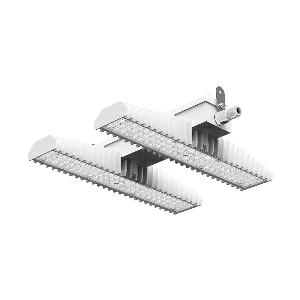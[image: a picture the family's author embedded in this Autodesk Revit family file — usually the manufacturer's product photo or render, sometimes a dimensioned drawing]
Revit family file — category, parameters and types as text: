
# Revit family: 3f_filippi_-_3f_lem_concentrato_3f_filippi_-_58888_-_3f_lem_2_led_100_cr_conc
name_source: partatom
category: Lighting Fixtures
units: mm (PartAtom-declared; Revit-internal decimal feet)

## family parameters
Cut with Voids When Loaded = No
Host = Face
Light Source = No
Part Type = Normal
Room Calculation Point = No
Round Connector Dimension = Use Diameter
Shared = No

## types (1)
- 3F Filippi - 3F LEM Concentrato (1 x LED, 16270 lm, 109 W, 4000 K)
    Apparent Load = 109 VA
    Approval mark = CE
    CIE Flux Codes = 83 96 99 100 100
    Color Rendering = 80
    Color Temperature = 4000 K
    Control Gear = Electronic ballast
    Default Elevation = 1800 mm
    Description = Industrial luminaire with high light output and high luminous efficiency designed with the most innovative technologies for environments with temperature up to 55°C.

ILLUMINOTECHNICAL
Luminous efficiency 100% (DLOR 100%, ULOR 0%).
Initial luminous flux of the luminaire 16270 lm.
Direct symmetric narrow distribution: the illuminated area has a elliptical shape.
Installation Interdistance Transv.D = 0.52 x hu - Long.D = 1.16 x hu.
Tabular UGR (CIE 117 - 4H-8H; S=0.25H; 70/50/20): RUG 16.8 - 20.6.
Beam angle: 31° - 73°.
Luminous efficacy 149 lm/W.
Lifetime (L93/B10): 30000 h. (tq+25°C)
Lifetime (L90/B10): 50000 h. (tq+25°C)
Lifetime (L85/B10): 80000 h. (tq+25°C)
Lifetime (L80/B10): 100000 h. (tq+25°C)
Lifetime (L85/B10): 50000 h. (tq+55°C)
Sudden decreased luminous flux after 50000 hours: 0% (C0).
Photobiological safety in compliance with IEC/TR 62778: RG0 risk exempt, (IEC 62471).
In compliance with IEC/EN 62722-2-1 - IEC/EN 62717 standards.

SOURCE
2 Mid-Power linear LED modules 50W/840.
Energy efficiency class (UE 2019/2020 - UE 2019/2015): C.
CIE 13.3 Colour rendering index: CRI >80 (R9 <50%).
IES TM-30 Fidelity Index: Rf = 84 Rg = 95.
CCT nominal colour temperature 4000 K.
Colour initial tolerance (MacAdam): SDCM 3.

MECHANICAL
Passive modular heatsinks in die-casted aluminium, painted in white colour.
To optimize the thermal management of the LED module, the heatsinks are oversized and provided with self-cleaning of cooling fins.
Wiring body in aluminium and galvanised steel anchored solidly to the sinks and thermally separated.
3F Lens lenses with high luminous efficiency, transparent methacrylate (PMMA), fixed to the LED modules.
Fixing brackets in stainless steel.
Luminaire with limited surface temperature. - D - (EN 60598-2-24)
Dimensions: 470x542 mm, height 129 mm. Weight 9.09 kg.
IP65 protection degree.
Mechanical strength to impacts IK06 (1 joule).
Glow-wire test resistance 650°C.

ELECTRICAL
Halogen Free electronic wiring 230V-50/60Hz, power factor 0.97, THD <25%, constant output current, class I, 1 driver.
Power of the luminaire 109 W.
ENEC - CE.
SAFE FLICKER: PstLM=<1 and SVM=<0.4 (IEC TR 61547-1 and IEC TR 63158), to ensure a more comfortable and safe light.
Luminaire compliant with EN 60598-2-22 for power supply from a centralised emergency system CPSS (Central Power Supply System), not incorporated in the luminaire - high risk areas excluded. The default power and flux are 100% in AC and 100% in DC.
Ambient temperature from -30°C to +55°C.
Temperature class T6 max 85°C.
Quick connection via M20 3P connector with 9-13 mm tightening range.
Power unit positioned on a separate compartment by the LED module to ensure optimum temperatures of cabling components, to be inspectable and maintainable.
Relative humidity UR: <85%.

INSTALLATION
Ceiling / Suspended / Wall.
All accessories dedicated to this product are available on the Catalog and on our website www.3F-Filippi.com.

APPLICATIONS
In commercial environments, exhibition and industrial areas, stores, open areas.
Applications with high ambient temperature up to 55°C.
Environments in which it is necessary a total protection against falling fragments (eg environments with foodstuffs or machines with moving parts or with extreme temperature changes), use luminaires with polycarbonate lenses.

WARNING
Fixture not suitable for cold stores with an ambient temperature <0°C and/or relative humidity >85%.
Luminaire designed for disposal/recycling at end-of-life.
Replaceable (LED only) light source by a professional. Replaceable control gear by a professional.
    Height = 129 mm
    Lamp = 1 x LED
    Lamp Light Flux = 16270 lm
    Lamp Power = 109 W
    Lamp count = 1
    Length = 470 mm
    Lifetime = 50000 h
    Luminous efficacy = 149 lm/W
    Manufacturer = 3F Filippi
    ModVariant = No
    Model = 3F Filippi - 58888 - 3F LEM 2 LED 100 CR CONC
    Mounting Place = Ceiling
    Mounting Type = Pendant
    Number of Poles = 1
    OnlyDefault = Yes
    Power Factor = 1
    Product Name = 3F Filippi - 3F LEM Concentrato
    Product group = pendant luminaire
    ProductGroupID = 9
    Protection Class = Protection class I
    Protection Degree = IP 65
    RLX_Detail_Level = 1
    RLX_Emergency_Light_Flux = 0 lm
    RLX_Emergency_Type = 0
    RLX_Emergency_Type_DB = No
    RlxData = <blob elided: 96625 chars, md5=1375702a>
    Socket = socket
    Standby Power = 0 W
    System Light Flux = 16270 lm
    System Power = 109 W
    Type Comments = Product without accessories
    Type Image = 3f_filippi_-_lem_2.jpg
    URL = http://relux.com
    VarID = ---
    Voltage = 0 V
    Weight = 0.00 kg
    Width = 542 mm

## geometry (parser evidence)
native form markers: Blend x4, Sweep x13
no freeform markers — native parametric forms only
